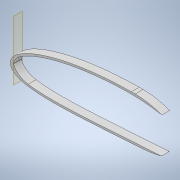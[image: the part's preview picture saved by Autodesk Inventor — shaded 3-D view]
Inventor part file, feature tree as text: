
AUTODESK INVENTOR PART (.ipt)
format: ipt  version: 2022.1 (Build 261234020, 234B)  size: 537,088 bytes
history: native  units: mm
features: sketch x6, extrude x5, thicken_offset x4, projected_geometry x3, shell x1, plane x1, other x1, fillet x1
ambient origin geometry x8: Origin, YZ Plane, XZ Plane, XY Plane, X Axis, Y Axis, Z Axis, Center Point
bodies: Solid1 (feature_tree)
feature tree (22):
  extrude  "Extrusion1"  Depth=3.0mm
  shell  "Shell1"  Thickness=1.0mm
  thicken_offset  "Thicken1"
  extrude  "Extrusion27"  TaperAngle=0.0deg  [1 undecoded]
  thicken_offset  "Thicken3"
  extrude  "Extrusion29"  Depth=20.0mm
  plane  "Work Plane5"
  other  "Bend Part2"
  thicken_offset  "Thicken5"
  extrude  "Extrusion30"  Depth=10.0mm TaperAngle=0.0deg
  thicken_offset  "Thicken6"
  extrude  "Extrusion31"  Depth=1.0mm
  fillet  "Fillet6"  Radius=1.0mm
  sketch  "Sketch3"  dims[d0=10.0mm d1=0.0mm d2=3.0mm d159=1.0mm d160=2.0mm]
  sketch  "Sketch48"  dims[d236=190.0mm d237=0.0mm d238=0.0mm]
  sketch  "Sketch55"  dims[d249=2.0mm d250=1.0mm d254=20.0mm]
  projected_geometry  "Projected Loop32"
  sketch  "Sketch57"  dims[d255=8.0mm d256=10.0mm d257=0.0mm]
  sketch  "Sketch58"  dims[d262=10.0mm d263=0.349066mm d264=1.0mm d265=1.0mm]
  projected_geometry  "Projected Loop34"
  sketch  "Sketch59"  dims[d268=50.0mm d269=3.0mm d270=10.0mm d271=0.0mm d272=2.5mm d273=2.0mm d274=3.0mm d275=200.0mm d276=10.0mm d277=0.0mm d278=100.0mm]
  projected_geometry  "Projected Loop35"
note: 1 required parameter value undecoded (feature->parameter linkage not recoverable at this tier; creation-order binding heuristic only, values carry confidence <= 0.55)
